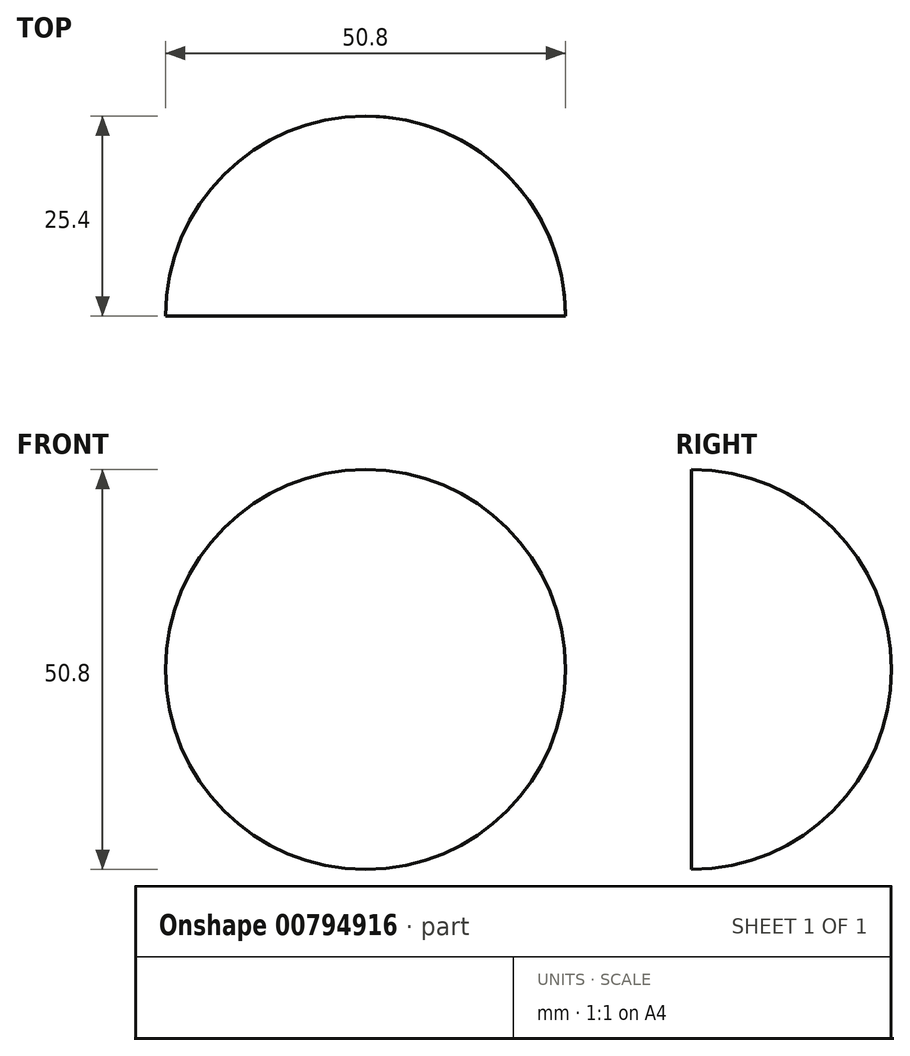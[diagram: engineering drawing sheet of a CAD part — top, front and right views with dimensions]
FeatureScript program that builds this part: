
annotation { "Feature Type Name" : "Feature", "Feature Type Description" : "" }
export const myFeature = defineFeature(function(context is Context, id is Id, definition is map)
    precondition{}
    {
        {
            var Q0;
            Q0=qCreatedBy(makeId("Top.planeOp"),FACE);
            var sketch = newSketch(context, id + "F0", { "sketchPlane" : qUnion([Q0])});
            skLineSegment(sketch, "E0", {"start": v(0, 0) * mm, "end": v(0, 25.4) * mm});
            skLineSegment(sketch, "E1", {"start": v(0, 0) * mm, "end": v(-25.4, 0) * mm});
            skLineSegment(sketch, "E2", {"start": v(0, 0) * mm, "end": v(25.4, 0) * mm});
            skArc(sketch, "E3", {"start": v(25.4, 0) * mm, "mid": v(0, 25.4) * mm, "end": v(-25.4, 0) * mm});
            skLineSegment(sketch, "E4", {"start": v(0, 0) * mm, "end": v(0, -25.4) * mm});
            skSolve(sketch);
        }
        {
            var Q0;
            {var subQ0=sQuery(id+"F0.wireOp",EDGE,"E0");Q0=makeQuery(id+"F0.imprint","IMPRINT",FACE,{"disambiguationData":[TD([[makeQuery(id+"F0.imprint","IMPRINT",EDGE,{"derivedFrom":subQ0}),1.0]])]});}
            var Q1;
            Q1=sQuery(id+"F0.wireOp",EDGE,"E0");
            revolve(context, id + "F1", {"surfaceOperationType" : NewSurfaceOperationType.NEW, "entities" : qUnion([Q0]), "axis" : qUnion([Q1]), "revolveType" : RevolveType.FULL});
        }
    });
